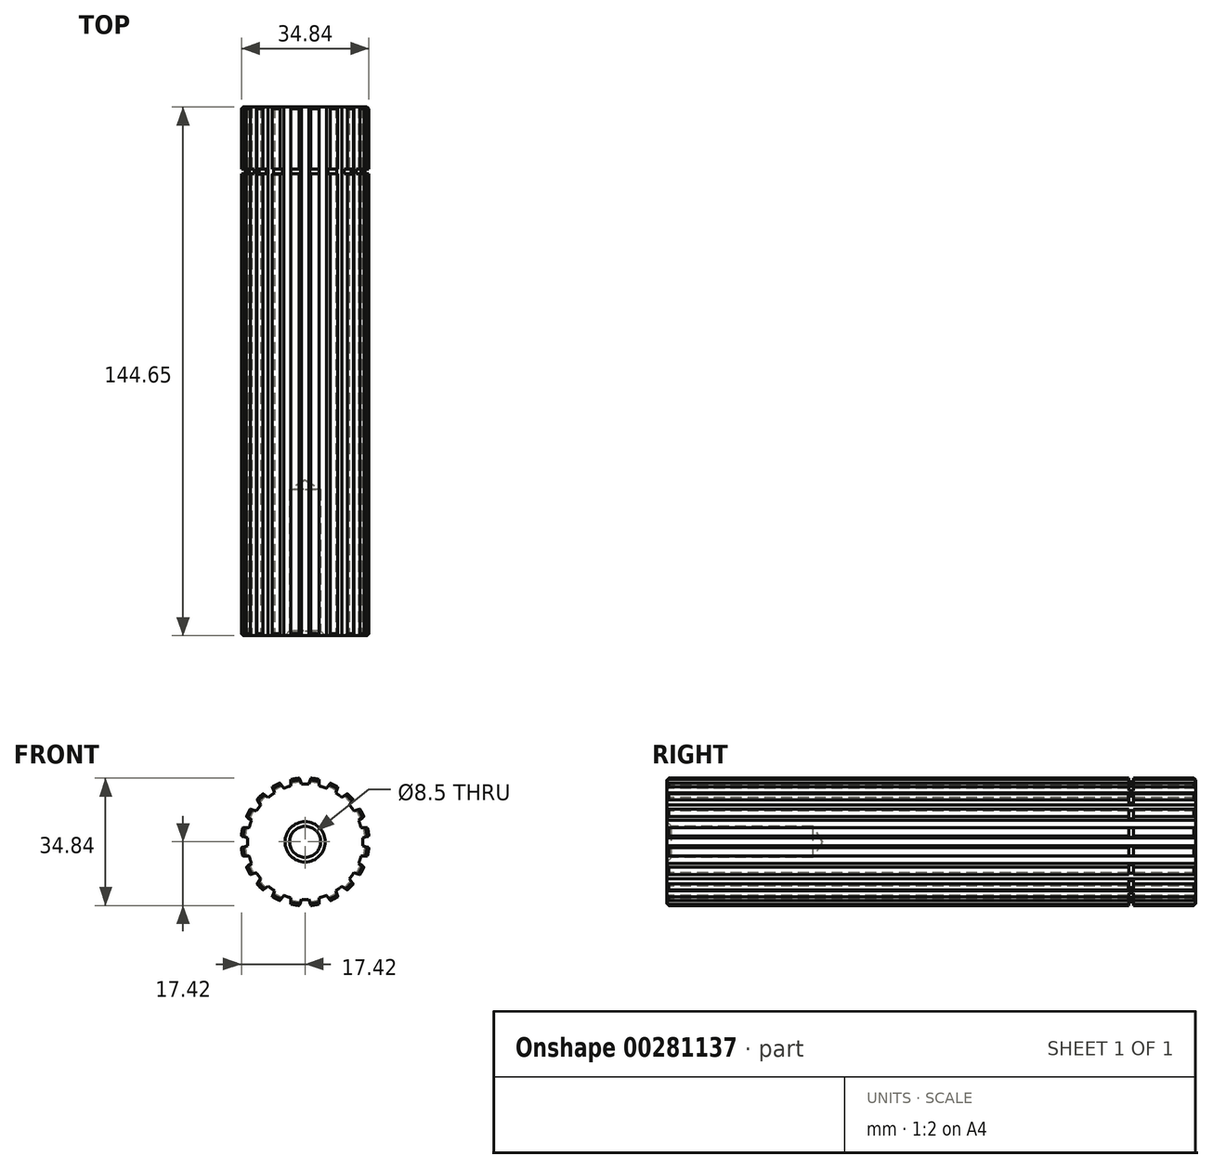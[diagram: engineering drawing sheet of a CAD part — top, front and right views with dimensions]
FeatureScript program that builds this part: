
annotation { "Feature Type Name" : "Feature", "Feature Type Description" : "" }
export const myFeature = defineFeature(function(context is Context, id is Id, definition is map)
    precondition{}
    {
        {
            var Q0;
            Q0=qCreatedBy(makeId("Front.planeOp"),FACE);
            var sketch = newSketch(context, id + "F0", { "sketchPlane" : qUnion([Q0])});
            skArc(sketch, "E0", {"start": v(-5.85, -14.65) * mm, "mid": v(-4.88, -15) * mm, "end": v(-3.88, -15.3) * mm});
            skLineSegment(sketch, "E1", {"start": v(-3.88, -15.3) * mm, "end": v(-3.88, -17.06) * mm});
            skLineSegment(sketch, "E2", {"start": v(-6.89, -16.08) * mm, "end": v(-5.85, -14.65) * mm});
            skArc(sketch, "E3", {"start": v(-3.88, -17.06) * mm, "mid": v(-2.74, -17.28) * mm, "end": v(-1.58, -17.42) * mm});
            skLineSegment(sketch, "E4", {"start": v(-1.58, -17.42) * mm, "end": v(-1.04, -15.75) * mm});
            skArc(sketch, "E5", {"start": v(-1.04, -15.75) * mm, "mid": v(0, -15.78) * mm, "end": v(1.04, -15.75) * mm});
            skLineSegment(sketch, "E6", {"start": v(1.04, -15.75) * mm, "end": v(1.58, -17.42) * mm});
            skArc(sketch, "E7", {"start": v(1.58, -17.42) * mm, "mid": v(2.74, -17.28) * mm, "end": v(3.88, -17.06) * mm});
            skLineSegment(sketch, "E8", {"start": v(3.88, -17.06) * mm, "end": v(3.88, -15.3) * mm});
            skArc(sketch, "E9", {"start": v(3.88, -15.3) * mm, "mid": v(4.88, -15) * mm, "end": v(5.85, -14.65) * mm});
            skLineSegment(sketch, "E10", {"start": v(5.85, -14.65) * mm, "end": v(6.89, -16.08) * mm});
            skArc(sketch, "E11", {"start": v(6.89, -16.08) * mm, "mid": v(7.94, -15.59) * mm, "end": v(8.96, -15.02) * mm});
            skLineSegment(sketch, "E12", {"start": v(8.96, -15.02) * mm, "end": v(8.42, -13.35) * mm});
            skArc(sketch, "E13", {"start": v(8.42, -13.35) * mm, "mid": v(9.28, -12.77) * mm, "end": v(10.1, -12.13) * mm});
            skLineSegment(sketch, "E14", {"start": v(10.1, -12.13) * mm, "end": v(11.52, -13.17) * mm});
            skArc(sketch, "E15", {"start": v(11.52, -13.17) * mm, "mid": v(12.37, -12.37) * mm, "end": v(13.17, -11.52) * mm});
            skLineSegment(sketch, "E16", {"start": v(13.17, -11.52) * mm, "end": v(12.13, -10.1) * mm});
            skArc(sketch, "E17", {"start": v(12.13, -10.1) * mm, "mid": v(12.77, -9.28) * mm, "end": v(13.35, -8.42) * mm});
            skLineSegment(sketch, "E18", {"start": v(13.35, -8.42) * mm, "end": v(15.02, -8.96) * mm});
            skArc(sketch, "E19", {"start": v(15.02, -8.96) * mm, "mid": v(15.59, -7.94) * mm, "end": v(16.08, -6.89) * mm});
            skLineSegment(sketch, "E20", {"start": v(16.08, -6.89) * mm, "end": v(14.65, -5.85) * mm});
            skArc(sketch, "E21", {"start": v(14.65, -5.85) * mm, "mid": v(15, -4.88) * mm, "end": v(15.3, -3.88) * mm});
            skLineSegment(sketch, "E22", {"start": v(15.3, -3.88) * mm, "end": v(17.06, -3.88) * mm});
            skArc(sketch, "E23", {"start": v(17.06, -3.88) * mm, "mid": v(17.28, -2.74) * mm, "end": v(17.42, -1.58) * mm});
            skLineSegment(sketch, "E24", {"start": v(17.42, -1.58) * mm, "end": v(15.75, -1.04) * mm});
            skArc(sketch, "E25", {"start": v(15.75, -1.04) * mm, "mid": v(15.78, 0) * mm, "end": v(15.75, 1.04) * mm});
            skLineSegment(sketch, "E26", {"start": v(15.75, 1.04) * mm, "end": v(17.42, 1.58) * mm});
            skArc(sketch, "E27", {"start": v(17.42, 1.58) * mm, "mid": v(17.28, 2.74) * mm, "end": v(17.06, 3.88) * mm});
            skLineSegment(sketch, "E28", {"start": v(17.06, 3.88) * mm, "end": v(15.3, 3.88) * mm});
            skArc(sketch, "E29", {"start": v(15.3, 3.88) * mm, "mid": v(15, 4.88) * mm, "end": v(14.65, 5.85) * mm});
            skLineSegment(sketch, "E30", {"start": v(14.65, 5.85) * mm, "end": v(16.08, 6.89) * mm});
            skArc(sketch, "E31", {"start": v(16.08, 6.89) * mm, "mid": v(15.59, 7.94) * mm, "end": v(15.02, 8.96) * mm});
            skLineSegment(sketch, "E32", {"start": v(15.02, 8.96) * mm, "end": v(13.35, 8.42) * mm});
            skArc(sketch, "E33", {"start": v(13.35, 8.42) * mm, "mid": v(12.77, 9.28) * mm, "end": v(12.13, 10.1) * mm});
            skLineSegment(sketch, "E34", {"start": v(12.13, 10.1) * mm, "end": v(13.17, 11.52) * mm});
            skArc(sketch, "E35", {"start": v(13.17, 11.52) * mm, "mid": v(12.37, 12.37) * mm, "end": v(11.52, 13.17) * mm});
            skLineSegment(sketch, "E36", {"start": v(11.52, 13.17) * mm, "end": v(10.1, 12.13) * mm});
            skArc(sketch, "E37", {"start": v(10.1, 12.13) * mm, "mid": v(9.28, 12.77) * mm, "end": v(8.42, 13.35) * mm});
            skLineSegment(sketch, "E38", {"start": v(8.42, 13.35) * mm, "end": v(8.96, 15.02) * mm});
            skArc(sketch, "E39", {"start": v(8.96, 15.02) * mm, "mid": v(7.94, 15.59) * mm, "end": v(6.89, 16.08) * mm});
            skLineSegment(sketch, "E40", {"start": v(6.89, 16.08) * mm, "end": v(5.85, 14.65) * mm});
            skArc(sketch, "E41", {"start": v(5.85, 14.65) * mm, "mid": v(4.88, 15) * mm, "end": v(3.88, 15.3) * mm});
            skLineSegment(sketch, "E42", {"start": v(3.88, 15.3) * mm, "end": v(3.88, 17.06) * mm});
            skArc(sketch, "E43", {"start": v(3.88, 17.06) * mm, "mid": v(2.74, 17.28) * mm, "end": v(1.58, 17.42) * mm});
            skLineSegment(sketch, "E44", {"start": v(1.58, 17.42) * mm, "end": v(1.04, 15.75) * mm});
            skArc(sketch, "E45", {"start": v(1.04, 15.75) * mm, "mid": v(0, 15.78) * mm, "end": v(-1.04, 15.75) * mm});
            skLineSegment(sketch, "E46", {"start": v(-1.04, 15.75) * mm, "end": v(-1.58, 17.42) * mm});
            skArc(sketch, "E47", {"start": v(-1.58, 17.42) * mm, "mid": v(-2.74, 17.28) * mm, "end": v(-3.88, 17.06) * mm});
            skLineSegment(sketch, "E48", {"start": v(-3.88, 17.06) * mm, "end": v(-3.88, 15.3) * mm});
            skArc(sketch, "E49", {"start": v(-3.88, 15.3) * mm, "mid": v(-4.88, 15) * mm, "end": v(-5.85, 14.65) * mm});
            skLineSegment(sketch, "E50", {"start": v(-5.85, 14.65) * mm, "end": v(-6.89, 16.08) * mm});
            skArc(sketch, "E51", {"start": v(-6.89, 16.08) * mm, "mid": v(-7.94, 15.59) * mm, "end": v(-8.96, 15.02) * mm});
            skLineSegment(sketch, "E52", {"start": v(-8.96, 15.02) * mm, "end": v(-8.42, 13.35) * mm});
            skArc(sketch, "E53", {"start": v(-8.42, 13.35) * mm, "mid": v(-9.28, 12.77) * mm, "end": v(-10.1, 12.13) * mm});
            skLineSegment(sketch, "E54", {"start": v(-10.1, 12.13) * mm, "end": v(-11.52, 13.17) * mm});
            skArc(sketch, "E55", {"start": v(-11.52, 13.17) * mm, "mid": v(-12.37, 12.37) * mm, "end": v(-13.17, 11.52) * mm});
            skLineSegment(sketch, "E56", {"start": v(-13.17, 11.52) * mm, "end": v(-12.13, 10.1) * mm});
            skArc(sketch, "E57", {"start": v(-12.13, 10.1) * mm, "mid": v(-12.77, 9.28) * mm, "end": v(-13.35, 8.42) * mm});
            skLineSegment(sketch, "E58", {"start": v(-13.35, 8.42) * mm, "end": v(-15.02, 8.96) * mm});
            skArc(sketch, "E59", {"start": v(-15.02, 8.96) * mm, "mid": v(-15.59, 7.94) * mm, "end": v(-16.08, 6.89) * mm});
            skLineSegment(sketch, "E60", {"start": v(-16.08, 6.89) * mm, "end": v(-14.65, 5.85) * mm});
            skArc(sketch, "E61", {"start": v(-14.65, 5.85) * mm, "mid": v(-15, 4.88) * mm, "end": v(-15.3, 3.88) * mm});
            skLineSegment(sketch, "E62", {"start": v(-15.3, 3.88) * mm, "end": v(-17.06, 3.88) * mm});
            skArc(sketch, "E63", {"start": v(-17.06, 3.88) * mm, "mid": v(-17.28, 2.74) * mm, "end": v(-17.42, 1.58) * mm});
            skLineSegment(sketch, "E64", {"start": v(-17.42, 1.58) * mm, "end": v(-15.75, 1.04) * mm});
            skArc(sketch, "E65", {"start": v(-15.75, 1.04) * mm, "mid": v(-15.78, 0) * mm, "end": v(-15.75, -1.04) * mm});
            skLineSegment(sketch, "E66", {"start": v(-15.75, -1.04) * mm, "end": v(-17.42, -1.58) * mm});
            skArc(sketch, "E67", {"start": v(-17.42, -1.58) * mm, "mid": v(-17.28, -2.74) * mm, "end": v(-17.06, -3.88) * mm});
            skLineSegment(sketch, "E68", {"start": v(-17.06, -3.88) * mm, "end": v(-15.3, -3.88) * mm});
            skArc(sketch, "E69", {"start": v(-15.3, -3.88) * mm, "mid": v(-15, -4.88) * mm, "end": v(-14.65, -5.85) * mm});
            skLineSegment(sketch, "E70", {"start": v(-14.65, -5.85) * mm, "end": v(-16.08, -6.89) * mm});
            skArc(sketch, "E71", {"start": v(-16.08, -6.89) * mm, "mid": v(-15.59, -7.94) * mm, "end": v(-15.02, -8.96) * mm});
            skLineSegment(sketch, "E72", {"start": v(-15.02, -8.96) * mm, "end": v(-13.35, -8.42) * mm});
            skArc(sketch, "E73", {"start": v(-13.35, -8.42) * mm, "mid": v(-12.77, -9.28) * mm, "end": v(-12.13, -10.1) * mm});
            skLineSegment(sketch, "E74", {"start": v(-12.13, -10.1) * mm, "end": v(-13.17, -11.52) * mm});
            skArc(sketch, "E75", {"start": v(-13.17, -11.52) * mm, "mid": v(-12.37, -12.37) * mm, "end": v(-11.52, -13.17) * mm});
            skLineSegment(sketch, "E76", {"start": v(-11.52, -13.17) * mm, "end": v(-10.1, -12.13) * mm});
            skArc(sketch, "E77", {"start": v(-10.1, -12.13) * mm, "mid": v(-9.28, -12.77) * mm, "end": v(-8.42, -13.35) * mm});
            skLineSegment(sketch, "E78", {"start": v(-8.42, -13.35) * mm, "end": v(-8.96, -15.02) * mm});
            skArc(sketch, "E79", {"start": v(-8.96, -15.02) * mm, "mid": v(-7.94, -15.59) * mm, "end": v(-6.89, -16.08) * mm});
            skLineSegment(sketch, "E80", {"start": v(0, -20.5) * mm, "end": v(0, 20.5) * mm, "construction": true});
            skLineSegment(sketch, "E81", {"start": v(-20.5, 0) * mm, "end": v(20.5, 0) * mm, "construction": true});
            skSolve(sketch);
        }
        {
            var Q0;
            Q0=qSketchRegion(id+"F0",true);
            extrude(context, id + "F1", {"entities" : qUnion([Q0]), "oppositeDirection" : true, "depth" : 144.65 * mm});
        }
        {
            var Q0;
            Q0=makeQuery(id+"Fq3001YINO4Uper_1.boolean.opBoolean","COPY",EDGE,{"derivedFrom":makeQuery(id+"Fq3001YINO4Uper_1.opExtrude","CAP_EDGE",EDGE,{"disambiguationData":[OSD([sQuery(id+"FlFwbRYxpEqd347_1.wireOp",EDGE,"EcN3jlIH-Wwh1-Q5Qi-RH9X-pUyHvn72nrl8")])],"isStart":true})});
            var Q1;
            Q1=makeQuery(id+"F1.opExtrude","CAP_EDGE",EDGE,{"disambiguationData":[OSD([sQuery(id+"F0.wireOp",EDGE,"E39")])],"isStart":false});
            var Q2;
            Q2=makeQuery(id+"F1.opExtrude","CAP_EDGE",EDGE,{"disambiguationData":[OSD([sQuery(id+"F0.wireOp",EDGE,"E43")])],"isStart":false});
            var Q3;
            Q3=makeQuery(id+"F1.opExtrude","CAP_EDGE",EDGE,{"disambiguationData":[OSD([sQuery(id+"F0.wireOp",EDGE,"E47")])],"isStart":false});
            var Q4;
            Q4=makeQuery(id+"F1.opExtrude","CAP_EDGE",EDGE,{"disambiguationData":[OSD([sQuery(id+"F0.wireOp",EDGE,"E35")])],"isStart":false});
            var Q5;
            Q5=makeQuery(id+"F1.opExtrude","CAP_EDGE",EDGE,{"disambiguationData":[OSD([sQuery(id+"F0.wireOp",EDGE,"E31")])],"isStart":false});
            var Q6;
            Q6=makeQuery(id+"F1.opExtrude","CAP_EDGE",EDGE,{"disambiguationData":[OSD([sQuery(id+"F0.wireOp",EDGE,"E27")])],"isStart":false});
            var Q7;
            Q7=makeQuery(id+"F1.opExtrude","CAP_EDGE",EDGE,{"disambiguationData":[OSD([sQuery(id+"F0.wireOp",EDGE,"E51")])],"isStart":false});
            var Q8;
            Q8=makeQuery(id+"F1.opExtrude","CAP_EDGE",EDGE,{"disambiguationData":[OSD([sQuery(id+"F0.wireOp",EDGE,"E55")])],"isStart":false});
            var Q9;
            Q9=makeQuery(id+"F1.opExtrude","CAP_EDGE",EDGE,{"disambiguationData":[OSD([sQuery(id+"F0.wireOp",EDGE,"E59")])],"isStart":false});
            var Q10;
            Q10=makeQuery(id+"F1.opExtrude","CAP_EDGE",EDGE,{"disambiguationData":[OSD([sQuery(id+"F0.wireOp",EDGE,"E63")])],"isStart":false});
            var Q11;
            Q11=makeQuery(id+"F1.opExtrude","CAP_EDGE",EDGE,{"disambiguationData":[OSD([sQuery(id+"F0.wireOp",EDGE,"E67")])],"isStart":false});
            var Q12;
            Q12=makeQuery(id+"F1.opExtrude","CAP_EDGE",EDGE,{"disambiguationData":[OSD([sQuery(id+"F0.wireOp",EDGE,"E71")])],"isStart":false});
            var Q13;
            Q13=makeQuery(id+"F1.opExtrude","CAP_EDGE",EDGE,{"disambiguationData":[OSD([sQuery(id+"F0.wireOp",EDGE,"E75")])],"isStart":false});
            var Q14;
            Q14=makeQuery(id+"F1.opExtrude","CAP_EDGE",EDGE,{"disambiguationData":[OSD([sQuery(id+"F0.wireOp",EDGE,"E79")])],"isStart":false});
            var Q15;
            Q15=makeQuery(id+"F1.opExtrude","CAP_EDGE",EDGE,{"disambiguationData":[OSD([sQuery(id+"F0.wireOp",EDGE,"E3")])],"isStart":false});
            var Q16;
            Q16=makeQuery(id+"F1.opExtrude","CAP_EDGE",EDGE,{"disambiguationData":[OSD([sQuery(id+"F0.wireOp",EDGE,"E7")])],"isStart":false});
            var Q17;
            Q17=makeQuery(id+"F1.opExtrude","CAP_EDGE",EDGE,{"disambiguationData":[OSD([sQuery(id+"F0.wireOp",EDGE,"E11")])],"isStart":false});
            var Q18;
            Q18=makeQuery(id+"F1.opExtrude","CAP_EDGE",EDGE,{"disambiguationData":[OSD([sQuery(id+"F0.wireOp",EDGE,"E15")])],"isStart":false});
            var Q19;
            Q19=makeQuery(id+"F1.opExtrude","CAP_EDGE",EDGE,{"disambiguationData":[OSD([sQuery(id+"F0.wireOp",EDGE,"E19")])],"isStart":false});
            var Q20;
            Q20=makeQuery(id+"F1.opExtrude","CAP_EDGE",EDGE,{"disambiguationData":[OSD([sQuery(id+"F0.wireOp",EDGE,"E23")])],"isStart":false});
            var Q21;
            Q21=makeQuery(id+"F1.opExtrude","CAP_EDGE",EDGE,{"disambiguationData":[OSD([sQuery(id+"F0.wireOp",EDGE,"E55")])],"isStart":true});
            var Q22;
            Q22=makeQuery(id+"F1.opExtrude","CAP_EDGE",EDGE,{"disambiguationData":[OSD([sQuery(id+"F0.wireOp",EDGE,"E51")])],"isStart":true});
            var Q23;
            Q23=makeQuery(id+"F1.opExtrude","CAP_EDGE",EDGE,{"disambiguationData":[OSD([sQuery(id+"F0.wireOp",EDGE,"E47")])],"isStart":true});
            var Q24;
            Q24=makeQuery(id+"F1.opExtrude","CAP_EDGE",EDGE,{"disambiguationData":[OSD([sQuery(id+"F0.wireOp",EDGE,"E59")])],"isStart":true});
            var Q25;
            Q25=makeQuery(id+"F1.opExtrude","CAP_EDGE",EDGE,{"disambiguationData":[OSD([sQuery(id+"F0.wireOp",EDGE,"E43")])],"isStart":true});
            var Q26;
            Q26=makeQuery(id+"F1.opExtrude","CAP_EDGE",EDGE,{"disambiguationData":[OSD([sQuery(id+"F0.wireOp",EDGE,"E39")])],"isStart":true});
            var Q27;
            Q27=makeQuery(id+"F1.opExtrude","CAP_EDGE",EDGE,{"disambiguationData":[OSD([sQuery(id+"F0.wireOp",EDGE,"E35")])],"isStart":true});
            var Q28;
            Q28=makeQuery(id+"F1.opExtrude","CAP_EDGE",EDGE,{"disambiguationData":[OSD([sQuery(id+"F0.wireOp",EDGE,"E31")])],"isStart":true});
            var Q29;
            Q29=makeQuery(id+"F1.opExtrude","CAP_EDGE",EDGE,{"disambiguationData":[OSD([sQuery(id+"F0.wireOp",EDGE,"E27")])],"isStart":true});
            var Q30;
            Q30=makeQuery(id+"F1.opExtrude","CAP_EDGE",EDGE,{"disambiguationData":[OSD([sQuery(id+"F0.wireOp",EDGE,"E23")])],"isStart":true});
            var Q31;
            Q31=makeQuery(id+"F1.opExtrude","CAP_EDGE",EDGE,{"disambiguationData":[OSD([sQuery(id+"F0.wireOp",EDGE,"E19")])],"isStart":true});
            var Q32;
            Q32=makeQuery(id+"F1.opExtrude","CAP_EDGE",EDGE,{"disambiguationData":[OSD([sQuery(id+"F0.wireOp",EDGE,"E15")])],"isStart":true});
            var Q33;
            Q33=makeQuery(id+"F1.opExtrude","CAP_EDGE",EDGE,{"disambiguationData":[OSD([sQuery(id+"F0.wireOp",EDGE,"E11")])],"isStart":true});
            var Q34;
            Q34=makeQuery(id+"F1.opExtrude","CAP_EDGE",EDGE,{"disambiguationData":[OSD([sQuery(id+"F0.wireOp",EDGE,"E7")])],"isStart":true});
            var Q35;
            Q35=makeQuery(id+"F1.opExtrude","CAP_EDGE",EDGE,{"disambiguationData":[OSD([sQuery(id+"F0.wireOp",EDGE,"E3")])],"isStart":true});
            var Q36;
            Q36=makeQuery(id+"F1.opExtrude","CAP_EDGE",EDGE,{"disambiguationData":[OSD([sQuery(id+"F0.wireOp",EDGE,"E79")])],"isStart":true});
            var Q37;
            Q37=makeQuery(id+"F1.opExtrude","CAP_EDGE",EDGE,{"disambiguationData":[OSD([sQuery(id+"F0.wireOp",EDGE,"E75")])],"isStart":true});
            var Q38;
            Q38=makeQuery(id+"F1.opExtrude","CAP_EDGE",EDGE,{"disambiguationData":[OSD([sQuery(id+"F0.wireOp",EDGE,"E71")])],"isStart":true});
            var Q39;
            Q39=makeQuery(id+"F1.opExtrude","CAP_EDGE",EDGE,{"disambiguationData":[OSD([sQuery(id+"F0.wireOp",EDGE,"E67")])],"isStart":true});
            var Q40;
            Q40=makeQuery(id+"F1.opExtrude","CAP_EDGE",EDGE,{"disambiguationData":[OSD([sQuery(id+"F0.wireOp",EDGE,"E63")])],"isStart":true});
            var Q41;
            Q41=makeQuery(id+"Fq3001YINO4Uper_1.boolean.opBoolean","INTERSECT",EDGE,{"derivedFrom":[makeQuery(id+"FyoZ7UQzVbIrVyw_1.hole-0.boolean.opBoolean","COPY",FACE,{"derivedFrom":makeQuery(id+"FyoZ7UQzVbIrVyw_1.hole-0.opRevolve","SWEPT_FACE",FACE,{"disambiguationData":[OSD([sQuery(id+"FyoZ7UQzVbIrVyw_1.hole-0.sketch.wireOp",EDGE,"core_line_2")])]})}),makeQuery(id+"Fq3001YINO4Uper_1.opExtrude","CAP_FACE",FACE,{"disambiguationData":[OSD([sQuery(id+"FlFwbRYxpEqd347_1.wireOp",EDGE,"EcN3jlIH-Wwh1-Q5Qi-RH9X-pUyHvn72nrl8")])],"isStart":false})]});
            chamfer(context, id + "F2", {"entities" : qUnion([Q0, Q1, Q2, Q3, Q4, Q5, Q6, Q7, Q8, Q9, Q10, Q11, Q12, Q13, Q14, Q15, Q16, Q17, Q18, Q19, Q20, Q21, Q22, Q23, Q24, Q25, Q26, Q27, Q28, Q29, Q30, Q31, Q32, Q33, Q34, Q35, Q36, Q37, Q38, Q39, Q40, Q41]), "width" : .5 * mm, "tangentPropagation" : true});
        }
        {
            var Q0;
            Q0=makeQuery(id+"F1.opExtrude","CAP_FACE",FACE,{"disambiguationData":[OSD([sQuery(id+"F0.wireOp",EDGE,"E0"),sQuery(id+"F0.wireOp",EDGE,"E1"),sQuery(id+"F0.wireOp",EDGE,"E2"),sQuery(id+"F0.wireOp",EDGE,"E3"),sQuery(id+"F0.wireOp",EDGE,"E4"),sQuery(id+"F0.wireOp",EDGE,"E5"),sQuery(id+"F0.wireOp",EDGE,"E6"),sQuery(id+"F0.wireOp",EDGE,"E7"),sQuery(id+"F0.wireOp",EDGE,"E8"),sQuery(id+"F0.wireOp",EDGE,"E9"),sQuery(id+"F0.wireOp",EDGE,"E10"),sQuery(id+"F0.wireOp",EDGE,"E11"),sQuery(id+"F0.wireOp",EDGE,"E12"),sQuery(id+"F0.wireOp",EDGE,"E13"),sQuery(id+"F0.wireOp",EDGE,"E14"),sQuery(id+"F0.wireOp",EDGE,"E15"),sQuery(id+"F0.wireOp",EDGE,"E16"),sQuery(id+"F0.wireOp",EDGE,"E17"),sQuery(id+"F0.wireOp",EDGE,"E18"),sQuery(id+"F0.wireOp",EDGE,"E19"),sQuery(id+"F0.wireOp",EDGE,"E20"),sQuery(id+"F0.wireOp",EDGE,"E21"),sQuery(id+"F0.wireOp",EDGE,"E22"),sQuery(id+"F0.wireOp",EDGE,"E23"),sQuery(id+"F0.wireOp",EDGE,"E24"),sQuery(id+"F0.wireOp",EDGE,"E25"),sQuery(id+"F0.wireOp",EDGE,"E26"),sQuery(id+"F0.wireOp",EDGE,"E27"),sQuery(id+"F0.wireOp",EDGE,"E28"),sQuery(id+"F0.wireOp",EDGE,"E29"),sQuery(id+"F0.wireOp",EDGE,"E30"),sQuery(id+"F0.wireOp",EDGE,"E31"),sQuery(id+"F0.wireOp",EDGE,"E32"),sQuery(id+"F0.wireOp",EDGE,"E33"),sQuery(id+"F0.wireOp",EDGE,"E34"),sQuery(id+"F0.wireOp",EDGE,"E35"),sQuery(id+"F0.wireOp",EDGE,"E36"),sQuery(id+"F0.wireOp",EDGE,"E37"),sQuery(id+"F0.wireOp",EDGE,"E38"),sQuery(id+"F0.wireOp",EDGE,"E39"),sQuery(id+"F0.wireOp",EDGE,"E40"),sQuery(id+"F0.wireOp",EDGE,"E41"),sQuery(id+"F0.wireOp",EDGE,"E42"),sQuery(id+"F0.wireOp",EDGE,"E43"),sQuery(id+"F0.wireOp",EDGE,"E44"),sQuery(id+"F0.wireOp",EDGE,"E45"),sQuery(id+"F0.wireOp",EDGE,"E46"),sQuery(id+"F0.wireOp",EDGE,"E47"),sQuery(id+"F0.wireOp",EDGE,"E48"),sQuery(id+"F0.wireOp",EDGE,"E49"),sQuery(id+"F0.wireOp",EDGE,"E50"),sQuery(id+"F0.wireOp",EDGE,"E51"),sQuery(id+"F0.wireOp",EDGE,"E52"),sQuery(id+"F0.wireOp",EDGE,"E53"),sQuery(id+"F0.wireOp",EDGE,"E54"),sQuery(id+"F0.wireOp",EDGE,"E55"),sQuery(id+"F0.wireOp",EDGE,"E56"),sQuery(id+"F0.wireOp",EDGE,"E57"),sQuery(id+"F0.wireOp",EDGE,"E58"),sQuery(id+"F0.wireOp",EDGE,"E59"),sQuery(id+"F0.wireOp",EDGE,"E60"),sQuery(id+"F0.wireOp",EDGE,"E61"),sQuery(id+"F0.wireOp",EDGE,"E62"),sQuery(id+"F0.wireOp",EDGE,"E63"),sQuery(id+"F0.wireOp",EDGE,"E64"),sQuery(id+"F0.wireOp",EDGE,"E65"),sQuery(id+"F0.wireOp",EDGE,"E66"),sQuery(id+"F0.wireOp",EDGE,"E67"),sQuery(id+"F0.wireOp",EDGE,"E68"),sQuery(id+"F0.wireOp",EDGE,"E69"),sQuery(id+"F0.wireOp",EDGE,"E70"),sQuery(id+"F0.wireOp",EDGE,"E71"),sQuery(id+"F0.wireOp",EDGE,"E72"),sQuery(id+"F0.wireOp",EDGE,"E73"),sQuery(id+"F0.wireOp",EDGE,"E74"),sQuery(id+"F0.wireOp",EDGE,"E75"),sQuery(id+"F0.wireOp",EDGE,"E76"),sQuery(id+"F0.wireOp",EDGE,"E77"),sQuery(id+"F0.wireOp",EDGE,"E78"),sQuery(id+"F0.wireOp",EDGE,"E79")])],"isStart":true});
            var sketch = newSketch(context, id + "F3", { "sketchPlane" : qUnion([Q0])});
            skPoint(sketch, "E82.0", {"position": v(0, 0) * mm});
            skSolve(sketch);
        }
        {
            var Q0;
            Q0=sQuery(id+"F3.wireOp",VERTEX,"E82.0");
            var Q1;
            Q1=makeQuery(id+"F1.opExtrude","SWEPT_BODY",BODY,{"disambiguationData":[OSD([sQuery(id+"F0.wireOp",EDGE,"E0"),sQuery(id+"F0.wireOp",EDGE,"E1"),sQuery(id+"F0.wireOp",EDGE,"E2"),sQuery(id+"F0.wireOp",EDGE,"E3"),sQuery(id+"F0.wireOp",EDGE,"E4"),sQuery(id+"F0.wireOp",EDGE,"E5"),sQuery(id+"F0.wireOp",EDGE,"E6"),sQuery(id+"F0.wireOp",EDGE,"E7"),sQuery(id+"F0.wireOp",EDGE,"E8"),sQuery(id+"F0.wireOp",EDGE,"E9"),sQuery(id+"F0.wireOp",EDGE,"E10"),sQuery(id+"F0.wireOp",EDGE,"E11"),sQuery(id+"F0.wireOp",EDGE,"E12"),sQuery(id+"F0.wireOp",EDGE,"E13"),sQuery(id+"F0.wireOp",EDGE,"E14"),sQuery(id+"F0.wireOp",EDGE,"E15"),sQuery(id+"F0.wireOp",EDGE,"E16"),sQuery(id+"F0.wireOp",EDGE,"E17"),sQuery(id+"F0.wireOp",EDGE,"E18"),sQuery(id+"F0.wireOp",EDGE,"E19"),sQuery(id+"F0.wireOp",EDGE,"E20"),sQuery(id+"F0.wireOp",EDGE,"E21"),sQuery(id+"F0.wireOp",EDGE,"E22"),sQuery(id+"F0.wireOp",EDGE,"E23"),sQuery(id+"F0.wireOp",EDGE,"E24"),sQuery(id+"F0.wireOp",EDGE,"E25"),sQuery(id+"F0.wireOp",EDGE,"E26"),sQuery(id+"F0.wireOp",EDGE,"E27"),sQuery(id+"F0.wireOp",EDGE,"E28"),sQuery(id+"F0.wireOp",EDGE,"E29"),sQuery(id+"F0.wireOp",EDGE,"E30"),sQuery(id+"F0.wireOp",EDGE,"E31"),sQuery(id+"F0.wireOp",EDGE,"E32"),sQuery(id+"F0.wireOp",EDGE,"E33"),sQuery(id+"F0.wireOp",EDGE,"E34"),sQuery(id+"F0.wireOp",EDGE,"E35"),sQuery(id+"F0.wireOp",EDGE,"E36"),sQuery(id+"F0.wireOp",EDGE,"E37"),sQuery(id+"F0.wireOp",EDGE,"E38"),sQuery(id+"F0.wireOp",EDGE,"E39"),sQuery(id+"F0.wireOp",EDGE,"E40"),sQuery(id+"F0.wireOp",EDGE,"E41"),sQuery(id+"F0.wireOp",EDGE,"E42"),sQuery(id+"F0.wireOp",EDGE,"E43"),sQuery(id+"F0.wireOp",EDGE,"E44"),sQuery(id+"F0.wireOp",EDGE,"E45"),sQuery(id+"F0.wireOp",EDGE,"E46"),sQuery(id+"F0.wireOp",EDGE,"E47"),sQuery(id+"F0.wireOp",EDGE,"E48"),sQuery(id+"F0.wireOp",EDGE,"E49"),sQuery(id+"F0.wireOp",EDGE,"E50"),sQuery(id+"F0.wireOp",EDGE,"E51"),sQuery(id+"F0.wireOp",EDGE,"E52"),sQuery(id+"F0.wireOp",EDGE,"E53"),sQuery(id+"F0.wireOp",EDGE,"E54"),sQuery(id+"F0.wireOp",EDGE,"E55"),sQuery(id+"F0.wireOp",EDGE,"E56"),sQuery(id+"F0.wireOp",EDGE,"E57"),sQuery(id+"F0.wireOp",EDGE,"E58"),sQuery(id+"F0.wireOp",EDGE,"E59"),sQuery(id+"F0.wireOp",EDGE,"E60"),sQuery(id+"F0.wireOp",EDGE,"E61"),sQuery(id+"F0.wireOp",EDGE,"E62"),sQuery(id+"F0.wireOp",EDGE,"E63"),sQuery(id+"F0.wireOp",EDGE,"E64"),sQuery(id+"F0.wireOp",EDGE,"E65"),sQuery(id+"F0.wireOp",EDGE,"E66"),sQuery(id+"F0.wireOp",EDGE,"E67"),sQuery(id+"F0.wireOp",EDGE,"E68"),sQuery(id+"F0.wireOp",EDGE,"E69"),sQuery(id+"F0.wireOp",EDGE,"E70"),sQuery(id+"F0.wireOp",EDGE,"E71"),sQuery(id+"F0.wireOp",EDGE,"E72"),sQuery(id+"F0.wireOp",EDGE,"E73"),sQuery(id+"F0.wireOp",EDGE,"E74"),sQuery(id+"F0.wireOp",EDGE,"E75"),sQuery(id+"F0.wireOp",EDGE,"E76"),sQuery(id+"F0.wireOp",EDGE,"E77"),sQuery(id+"F0.wireOp",EDGE,"E78"),sQuery(id+"F0.wireOp",EDGE,"E79")])]});
            hole(context, id + "F4", {"style" : HoleStyle.C_SINK, "endStyle" : HoleEndStyle.BLIND, "holeDiameter" : 8.5 * mm, "cSinkDiameter" : 11 * mm, "cSinkAngle" : 90 * degree, "holeDepth" : 40 * mm, "tappedDepth" : 35.5 * mm, "tapClearance" : 3, "locations" : qUnion([Q0]), "scope" : qUnion([Q1])});
        }
        {
            var Q0;
            Q0=qCreatedBy(makeId("Front.planeOp"),FACE);
            cPlane(context, id + "F5", {"entities" : qUnion([Q0]), "cplaneType" : CPlaneType.OFFSET, "offset" : 126.35 * mm, "oppositeDirection" : true, "width" : 150 * mm, "height" : 150 * mm});
        }
        {
            var Q0;
            Q0=qCreatedBy(id+"F5.planeOp",FACE);
            var sketch = newSketch(context, id + "F6", { "sketchPlane" : qUnion([Q0])});
            skCircle(sketch, "E83", {"center": v(0, 0) * mm, "radius": 17.5 * mm});
            skCircle(sketch, "E84", {"center": v(0, 0) * mm, "radius": 16.45 * mm});
            skSolve(sketch);
        }
        {
            var Q0;
            Q0=makeQuery(id+"F6.imprint","IMPRINT",FACE,{"disambiguationData":[TD([[makeQuery(id+"F6.imprint","IMPRINT",EDGE,{"derivedFrom":sQuery(id+"F6.wireOp",EDGE,"E83")}),1.0]])]});
            extrude(context, id + "F7", {"entities" : qUnion([Q0]), "operationType" : NewBodyOperationType.REMOVE, "oppositeDirection" : true, "depth" : 1.3 * mm});
        }
        {
            var Q0;
            {var subQ0=sQuery(id+"F6.wireOp",EDGE,"E83");Q0=makeQuery(id+"F7.boolean.opBoolean","COPY",EDGE,{"disambiguationData":[topologyDisambiguationEdgeConnected([makeQuery(id+"F1.opExtrude","SWEPT_FACE",FACE,{"disambiguationData":[OSD([sQuery(id+"F0.wireOp",EDGE,"E39")])]})])],"derivedFrom":makeQuery(id+"F7.opExtrude","CAP_EDGE",EDGE,{"disambiguationData":[OSD([subQ0])],"isStart":true})});}
            var Q1;
            {var subQ0=sQuery(id+"F6.wireOp",EDGE,"E83");Q1=makeQuery(id+"F7.boolean.opBoolean","COPY",EDGE,{"disambiguationData":[topologyDisambiguationEdgeConnected([makeQuery(id+"F1.opExtrude","SWEPT_FACE",FACE,{"disambiguationData":[OSD([sQuery(id+"F0.wireOp",EDGE,"E39")])]})])],"derivedFrom":makeQuery(id+"F7.opExtrude","CAP_EDGE",EDGE,{"disambiguationData":[OSD([subQ0])],"isStart":false})});}
            var Q2;
            {var subQ0=sQuery(id+"F6.wireOp",EDGE,"E83");Q2=makeQuery(id+"F7.boolean.opBoolean","COPY",EDGE,{"disambiguationData":[topologyDisambiguationEdgeConnected([makeQuery(id+"F1.opExtrude","SWEPT_FACE",FACE,{"disambiguationData":[OSD([sQuery(id+"F0.wireOp",EDGE,"E43")])]})])],"derivedFrom":makeQuery(id+"F7.opExtrude","CAP_EDGE",EDGE,{"disambiguationData":[OSD([subQ0])],"isStart":true})});}
            var Q3;
            {var subQ0=sQuery(id+"F6.wireOp",EDGE,"E83");Q3=makeQuery(id+"F7.boolean.opBoolean","COPY",EDGE,{"disambiguationData":[topologyDisambiguationEdgeConnected([makeQuery(id+"F1.opExtrude","SWEPT_FACE",FACE,{"disambiguationData":[OSD([sQuery(id+"F0.wireOp",EDGE,"E43")])]})])],"derivedFrom":makeQuery(id+"F7.opExtrude","CAP_EDGE",EDGE,{"disambiguationData":[OSD([subQ0])],"isStart":false})});}
            var Q4;
            {var subQ0=sQuery(id+"F6.wireOp",EDGE,"E83");Q4=makeQuery(id+"F7.boolean.opBoolean","COPY",EDGE,{"disambiguationData":[topologyDisambiguationEdgeConnected([makeQuery(id+"F1.opExtrude","SWEPT_FACE",FACE,{"disambiguationData":[OSD([sQuery(id+"F0.wireOp",EDGE,"E47")])]})])],"derivedFrom":makeQuery(id+"F7.opExtrude","CAP_EDGE",EDGE,{"disambiguationData":[OSD([subQ0])],"isStart":false})});}
            var Q5;
            {var subQ0=sQuery(id+"F6.wireOp",EDGE,"E83");Q5=makeQuery(id+"F7.boolean.opBoolean","COPY",EDGE,{"disambiguationData":[topologyDisambiguationEdgeConnected([makeQuery(id+"F1.opExtrude","SWEPT_FACE",FACE,{"disambiguationData":[OSD([sQuery(id+"F0.wireOp",EDGE,"E47")])]})])],"derivedFrom":makeQuery(id+"F7.opExtrude","CAP_EDGE",EDGE,{"disambiguationData":[OSD([subQ0])],"isStart":true})});}
            var Q6;
            {var subQ0=sQuery(id+"F6.wireOp",EDGE,"E83");Q6=makeQuery(id+"F7.boolean.opBoolean","COPY",EDGE,{"disambiguationData":[topologyDisambiguationEdgeConnected([makeQuery(id+"F1.opExtrude","SWEPT_FACE",FACE,{"disambiguationData":[OSD([sQuery(id+"F0.wireOp",EDGE,"E35")])]})])],"derivedFrom":makeQuery(id+"F7.opExtrude","CAP_EDGE",EDGE,{"disambiguationData":[OSD([subQ0])],"isStart":false})});}
            var Q7;
            {var subQ0=sQuery(id+"F6.wireOp",EDGE,"E83");Q7=makeQuery(id+"F7.boolean.opBoolean","COPY",EDGE,{"disambiguationData":[topologyDisambiguationEdgeConnected([makeQuery(id+"F1.opExtrude","SWEPT_FACE",FACE,{"disambiguationData":[OSD([sQuery(id+"F0.wireOp",EDGE,"E35")])]})])],"derivedFrom":makeQuery(id+"F7.opExtrude","CAP_EDGE",EDGE,{"disambiguationData":[OSD([subQ0])],"isStart":true})});}
            var Q8;
            {var subQ0=sQuery(id+"F6.wireOp",EDGE,"E83");Q8=makeQuery(id+"F7.boolean.opBoolean","COPY",EDGE,{"disambiguationData":[topologyDisambiguationEdgeConnected([makeQuery(id+"F1.opExtrude","SWEPT_FACE",FACE,{"disambiguationData":[OSD([sQuery(id+"F0.wireOp",EDGE,"E51")])]})])],"derivedFrom":makeQuery(id+"F7.opExtrude","CAP_EDGE",EDGE,{"disambiguationData":[OSD([subQ0])],"isStart":false})});}
            var Q9;
            {var subQ0=sQuery(id+"F6.wireOp",EDGE,"E83");Q9=makeQuery(id+"F7.boolean.opBoolean","COPY",EDGE,{"disambiguationData":[topologyDisambiguationEdgeConnected([makeQuery(id+"F1.opExtrude","SWEPT_FACE",FACE,{"disambiguationData":[OSD([sQuery(id+"F0.wireOp",EDGE,"E51")])]})])],"derivedFrom":makeQuery(id+"F7.opExtrude","CAP_EDGE",EDGE,{"disambiguationData":[OSD([subQ0])],"isStart":true})});}
            var Q10;
            {var subQ0=sQuery(id+"F6.wireOp",EDGE,"E83");Q10=makeQuery(id+"F7.boolean.opBoolean","COPY",EDGE,{"disambiguationData":[topologyDisambiguationEdgeConnected([makeQuery(id+"F1.opExtrude","SWEPT_FACE",FACE,{"disambiguationData":[OSD([sQuery(id+"F0.wireOp",EDGE,"E55")])]})])],"derivedFrom":makeQuery(id+"F7.opExtrude","CAP_EDGE",EDGE,{"disambiguationData":[OSD([subQ0])],"isStart":false})});}
            var Q11;
            {var subQ0=sQuery(id+"F6.wireOp",EDGE,"E83");Q11=makeQuery(id+"F7.boolean.opBoolean","COPY",EDGE,{"disambiguationData":[topologyDisambiguationEdgeConnected([makeQuery(id+"F1.opExtrude","SWEPT_FACE",FACE,{"disambiguationData":[OSD([sQuery(id+"F0.wireOp",EDGE,"E55")])]})])],"derivedFrom":makeQuery(id+"F7.opExtrude","CAP_EDGE",EDGE,{"disambiguationData":[OSD([subQ0])],"isStart":true})});}
            var Q12;
            {var subQ0=sQuery(id+"F6.wireOp",EDGE,"E83");Q12=makeQuery(id+"F7.boolean.opBoolean","COPY",EDGE,{"disambiguationData":[topologyDisambiguationEdgeConnected([makeQuery(id+"F1.opExtrude","SWEPT_FACE",FACE,{"disambiguationData":[OSD([sQuery(id+"F0.wireOp",EDGE,"E59")])]})])],"derivedFrom":makeQuery(id+"F7.opExtrude","CAP_EDGE",EDGE,{"disambiguationData":[OSD([subQ0])],"isStart":false})});}
            var Q13;
            {var subQ0=sQuery(id+"F6.wireOp",EDGE,"E83");Q13=makeQuery(id+"F7.boolean.opBoolean","COPY",EDGE,{"disambiguationData":[topologyDisambiguationEdgeConnected([makeQuery(id+"F1.opExtrude","SWEPT_FACE",FACE,{"disambiguationData":[OSD([sQuery(id+"F0.wireOp",EDGE,"E59")])]})])],"derivedFrom":makeQuery(id+"F7.opExtrude","CAP_EDGE",EDGE,{"disambiguationData":[OSD([subQ0])],"isStart":true})});}
            var Q14;
            {var subQ0=sQuery(id+"F6.wireOp",EDGE,"E83");Q14=makeQuery(id+"F7.boolean.opBoolean","COPY",EDGE,{"disambiguationData":[topologyDisambiguationEdgeConnected([makeQuery(id+"F1.opExtrude","SWEPT_FACE",FACE,{"disambiguationData":[OSD([sQuery(id+"F0.wireOp",EDGE,"E63")])]})])],"derivedFrom":makeQuery(id+"F7.opExtrude","CAP_EDGE",EDGE,{"disambiguationData":[OSD([subQ0])],"isStart":false})});}
            var Q15;
            {var subQ0=sQuery(id+"F6.wireOp",EDGE,"E83");Q15=makeQuery(id+"F7.boolean.opBoolean","COPY",EDGE,{"disambiguationData":[topologyDisambiguationEdgeConnected([makeQuery(id+"F1.opExtrude","SWEPT_FACE",FACE,{"disambiguationData":[OSD([sQuery(id+"F0.wireOp",EDGE,"E63")])]})])],"derivedFrom":makeQuery(id+"F7.opExtrude","CAP_EDGE",EDGE,{"disambiguationData":[OSD([subQ0])],"isStart":true})});}
            var Q16;
            {var subQ0=sQuery(id+"F6.wireOp",EDGE,"E83");Q16=makeQuery(id+"F7.boolean.opBoolean","COPY",EDGE,{"disambiguationData":[topologyDisambiguationEdgeConnected([makeQuery(id+"F1.opExtrude","SWEPT_FACE",FACE,{"disambiguationData":[OSD([sQuery(id+"F0.wireOp",EDGE,"E67")])]})])],"derivedFrom":makeQuery(id+"F7.opExtrude","CAP_EDGE",EDGE,{"disambiguationData":[OSD([subQ0])],"isStart":false})});}
            var Q17;
            {var subQ0=sQuery(id+"F6.wireOp",EDGE,"E83");Q17=makeQuery(id+"F7.boolean.opBoolean","COPY",EDGE,{"disambiguationData":[topologyDisambiguationEdgeConnected([makeQuery(id+"F1.opExtrude","SWEPT_FACE",FACE,{"disambiguationData":[OSD([sQuery(id+"F0.wireOp",EDGE,"E67")])]})])],"derivedFrom":makeQuery(id+"F7.opExtrude","CAP_EDGE",EDGE,{"disambiguationData":[OSD([subQ0])],"isStart":true})});}
            var Q18;
            {var subQ0=sQuery(id+"F6.wireOp",EDGE,"E83");Q18=makeQuery(id+"F7.boolean.opBoolean","COPY",EDGE,{"disambiguationData":[topologyDisambiguationEdgeConnected([makeQuery(id+"F1.opExtrude","SWEPT_FACE",FACE,{"disambiguationData":[OSD([sQuery(id+"F0.wireOp",EDGE,"E71")])]})])],"derivedFrom":makeQuery(id+"F7.opExtrude","CAP_EDGE",EDGE,{"disambiguationData":[OSD([subQ0])],"isStart":false})});}
            var Q19;
            {var subQ0=sQuery(id+"F6.wireOp",EDGE,"E83");Q19=makeQuery(id+"F7.boolean.opBoolean","COPY",EDGE,{"disambiguationData":[topologyDisambiguationEdgeConnected([makeQuery(id+"F1.opExtrude","SWEPT_FACE",FACE,{"disambiguationData":[OSD([sQuery(id+"F0.wireOp",EDGE,"E71")])]})])],"derivedFrom":makeQuery(id+"F7.opExtrude","CAP_EDGE",EDGE,{"disambiguationData":[OSD([subQ0])],"isStart":true})});}
            var Q20;
            {var subQ0=sQuery(id+"F6.wireOp",EDGE,"E83");Q20=makeQuery(id+"F7.boolean.opBoolean","COPY",EDGE,{"disambiguationData":[topologyDisambiguationEdgeConnected([makeQuery(id+"F1.opExtrude","SWEPT_FACE",FACE,{"disambiguationData":[OSD([sQuery(id+"F0.wireOp",EDGE,"E75")])]})])],"derivedFrom":makeQuery(id+"F7.opExtrude","CAP_EDGE",EDGE,{"disambiguationData":[OSD([subQ0])],"isStart":false})});}
            var Q21;
            {var subQ0=sQuery(id+"F6.wireOp",EDGE,"E83");Q21=makeQuery(id+"F7.boolean.opBoolean","COPY",EDGE,{"disambiguationData":[topologyDisambiguationEdgeConnected([makeQuery(id+"F1.opExtrude","SWEPT_FACE",FACE,{"disambiguationData":[OSD([sQuery(id+"F0.wireOp",EDGE,"E75")])]})])],"derivedFrom":makeQuery(id+"F7.opExtrude","CAP_EDGE",EDGE,{"disambiguationData":[OSD([subQ0])],"isStart":true})});}
            var Q22;
            {var subQ0=sQuery(id+"F6.wireOp",EDGE,"E83");Q22=makeQuery(id+"F7.boolean.opBoolean","COPY",EDGE,{"disambiguationData":[topologyDisambiguationEdgeConnected([makeQuery(id+"F1.opExtrude","SWEPT_FACE",FACE,{"disambiguationData":[OSD([sQuery(id+"F0.wireOp",EDGE,"E79")])]})])],"derivedFrom":makeQuery(id+"F7.opExtrude","CAP_EDGE",EDGE,{"disambiguationData":[OSD([subQ0])],"isStart":false})});}
            var Q23;
            {var subQ0=sQuery(id+"F6.wireOp",EDGE,"E83");Q23=makeQuery(id+"F7.boolean.opBoolean","COPY",EDGE,{"disambiguationData":[topologyDisambiguationEdgeConnected([makeQuery(id+"F1.opExtrude","SWEPT_FACE",FACE,{"disambiguationData":[OSD([sQuery(id+"F0.wireOp",EDGE,"E79")])]})])],"derivedFrom":makeQuery(id+"F7.opExtrude","CAP_EDGE",EDGE,{"disambiguationData":[OSD([subQ0])],"isStart":true})});}
            var Q24;
            {var subQ0=sQuery(id+"F6.wireOp",EDGE,"E83");Q24=makeQuery(id+"F7.boolean.opBoolean","COPY",EDGE,{"disambiguationData":[topologyDisambiguationEdgeConnected([makeQuery(id+"F1.opExtrude","SWEPT_FACE",FACE,{"disambiguationData":[OSD([sQuery(id+"F0.wireOp",EDGE,"E3")])]})])],"derivedFrom":makeQuery(id+"F7.opExtrude","CAP_EDGE",EDGE,{"disambiguationData":[OSD([subQ0])],"isStart":false})});}
            var Q25;
            {var subQ0=sQuery(id+"F6.wireOp",EDGE,"E83");Q25=makeQuery(id+"F7.boolean.opBoolean","COPY",EDGE,{"disambiguationData":[topologyDisambiguationEdgeConnected([makeQuery(id+"F1.opExtrude","SWEPT_FACE",FACE,{"disambiguationData":[OSD([sQuery(id+"F0.wireOp",EDGE,"E3")])]})])],"derivedFrom":makeQuery(id+"F7.opExtrude","CAP_EDGE",EDGE,{"disambiguationData":[OSD([subQ0])],"isStart":true})});}
            var Q26;
            {var subQ0=sQuery(id+"F6.wireOp",EDGE,"E83");Q26=makeQuery(id+"F7.boolean.opBoolean","COPY",EDGE,{"disambiguationData":[topologyDisambiguationEdgeConnected([makeQuery(id+"F1.opExtrude","SWEPT_FACE",FACE,{"disambiguationData":[OSD([sQuery(id+"F0.wireOp",EDGE,"E7")])]})])],"derivedFrom":makeQuery(id+"F7.opExtrude","CAP_EDGE",EDGE,{"disambiguationData":[OSD([subQ0])],"isStart":false})});}
            var Q27;
            {var subQ0=sQuery(id+"F6.wireOp",EDGE,"E83");Q27=makeQuery(id+"F7.boolean.opBoolean","COPY",EDGE,{"disambiguationData":[topologyDisambiguationEdgeConnected([makeQuery(id+"F1.opExtrude","SWEPT_FACE",FACE,{"disambiguationData":[OSD([sQuery(id+"F0.wireOp",EDGE,"E11")])]})])],"derivedFrom":makeQuery(id+"F7.opExtrude","CAP_EDGE",EDGE,{"disambiguationData":[OSD([subQ0])],"isStart":true})});}
            var Q28;
            {var subQ0=sQuery(id+"F6.wireOp",EDGE,"E83");Q28=makeQuery(id+"F7.boolean.opBoolean","COPY",EDGE,{"disambiguationData":[topologyDisambiguationEdgeConnected([makeQuery(id+"F1.opExtrude","SWEPT_FACE",FACE,{"disambiguationData":[OSD([sQuery(id+"F0.wireOp",EDGE,"E15")])]})])],"derivedFrom":makeQuery(id+"F7.opExtrude","CAP_EDGE",EDGE,{"disambiguationData":[OSD([subQ0])],"isStart":false})});}
            var Q29;
            {var subQ0=sQuery(id+"F6.wireOp",EDGE,"E83");Q29=makeQuery(id+"F7.boolean.opBoolean","COPY",EDGE,{"disambiguationData":[topologyDisambiguationEdgeConnected([makeQuery(id+"F1.opExtrude","SWEPT_FACE",FACE,{"disambiguationData":[OSD([sQuery(id+"F0.wireOp",EDGE,"E15")])]})])],"derivedFrom":makeQuery(id+"F7.opExtrude","CAP_EDGE",EDGE,{"disambiguationData":[OSD([subQ0])],"isStart":true})});}
            var Q30;
            {var subQ0=sQuery(id+"F6.wireOp",EDGE,"E83");Q30=makeQuery(id+"F7.boolean.opBoolean","COPY",EDGE,{"disambiguationData":[topologyDisambiguationEdgeConnected([makeQuery(id+"F1.opExtrude","SWEPT_FACE",FACE,{"disambiguationData":[OSD([sQuery(id+"F0.wireOp",EDGE,"E31")])]})])],"derivedFrom":makeQuery(id+"F7.opExtrude","CAP_EDGE",EDGE,{"disambiguationData":[OSD([subQ0])],"isStart":true})});}
            var Q31;
            {var subQ0=sQuery(id+"F6.wireOp",EDGE,"E83");Q31=makeQuery(id+"F7.boolean.opBoolean","COPY",EDGE,{"disambiguationData":[topologyDisambiguationEdgeConnected([makeQuery(id+"F1.opExtrude","SWEPT_FACE",FACE,{"disambiguationData":[OSD([sQuery(id+"F0.wireOp",EDGE,"E31")])]})])],"derivedFrom":makeQuery(id+"F7.opExtrude","CAP_EDGE",EDGE,{"disambiguationData":[OSD([subQ0])],"isStart":false})});}
            var Q32;
            {var subQ0=sQuery(id+"F6.wireOp",EDGE,"E83");Q32=makeQuery(id+"F7.boolean.opBoolean","COPY",EDGE,{"disambiguationData":[topologyDisambiguationEdgeConnected([makeQuery(id+"F1.opExtrude","SWEPT_FACE",FACE,{"disambiguationData":[OSD([sQuery(id+"F0.wireOp",EDGE,"E27")])]})])],"derivedFrom":makeQuery(id+"F7.opExtrude","CAP_EDGE",EDGE,{"disambiguationData":[OSD([subQ0])],"isStart":false})});}
            var Q33;
            {var subQ0=sQuery(id+"F6.wireOp",EDGE,"E83");Q33=makeQuery(id+"F7.boolean.opBoolean","COPY",EDGE,{"disambiguationData":[topologyDisambiguationEdgeConnected([makeQuery(id+"F1.opExtrude","SWEPT_FACE",FACE,{"disambiguationData":[OSD([sQuery(id+"F0.wireOp",EDGE,"E27")])]})])],"derivedFrom":makeQuery(id+"F7.opExtrude","CAP_EDGE",EDGE,{"disambiguationData":[OSD([subQ0])],"isStart":true})});}
            var Q34;
            {var subQ0=sQuery(id+"F6.wireOp",EDGE,"E83");Q34=makeQuery(id+"F7.boolean.opBoolean","COPY",EDGE,{"disambiguationData":[topologyDisambiguationEdgeConnected([makeQuery(id+"F1.opExtrude","SWEPT_FACE",FACE,{"disambiguationData":[OSD([sQuery(id+"F0.wireOp",EDGE,"E23")])]})])],"derivedFrom":makeQuery(id+"F7.opExtrude","CAP_EDGE",EDGE,{"disambiguationData":[OSD([subQ0])],"isStart":true})});}
            var Q35;
            {var subQ0=sQuery(id+"F6.wireOp",EDGE,"E83");Q35=makeQuery(id+"F7.boolean.opBoolean","COPY",EDGE,{"disambiguationData":[topologyDisambiguationEdgeConnected([makeQuery(id+"F1.opExtrude","SWEPT_FACE",FACE,{"disambiguationData":[OSD([sQuery(id+"F0.wireOp",EDGE,"E23")])]})])],"derivedFrom":makeQuery(id+"F7.opExtrude","CAP_EDGE",EDGE,{"disambiguationData":[OSD([subQ0])],"isStart":false})});}
            var Q36;
            {var subQ0=sQuery(id+"F6.wireOp",EDGE,"E83");Q36=makeQuery(id+"F7.boolean.opBoolean","COPY",EDGE,{"disambiguationData":[topologyDisambiguationEdgeConnected([makeQuery(id+"F1.opExtrude","SWEPT_FACE",FACE,{"disambiguationData":[OSD([sQuery(id+"F0.wireOp",EDGE,"E19")])]})])],"derivedFrom":makeQuery(id+"F7.opExtrude","CAP_EDGE",EDGE,{"disambiguationData":[OSD([subQ0])],"isStart":false})});}
            var Q37;
            {var subQ0=sQuery(id+"F6.wireOp",EDGE,"E83");Q37=makeQuery(id+"F7.boolean.opBoolean","COPY",EDGE,{"disambiguationData":[topologyDisambiguationEdgeConnected([makeQuery(id+"F1.opExtrude","SWEPT_FACE",FACE,{"disambiguationData":[OSD([sQuery(id+"F0.wireOp",EDGE,"E19")])]})])],"derivedFrom":makeQuery(id+"F7.opExtrude","CAP_EDGE",EDGE,{"disambiguationData":[OSD([subQ0])],"isStart":true})});}
            chamfer(context, id + "F8", {"entities" : qUnion([Q0, Q1, Q2, Q3, Q4, Q5, Q6, Q7, Q8, Q9, Q10, Q11, Q12, Q13, Q14, Q15, Q16, Q17, Q18, Q19, Q20, Q21, Q22, Q23, Q24, Q25, Q26, Q27, Q28, Q29, Q30, Q31, Q32, Q33, Q34, Q35, Q36, Q37]), "width" : .1 * mm, "tangentPropagation" : true});
        }
    });
